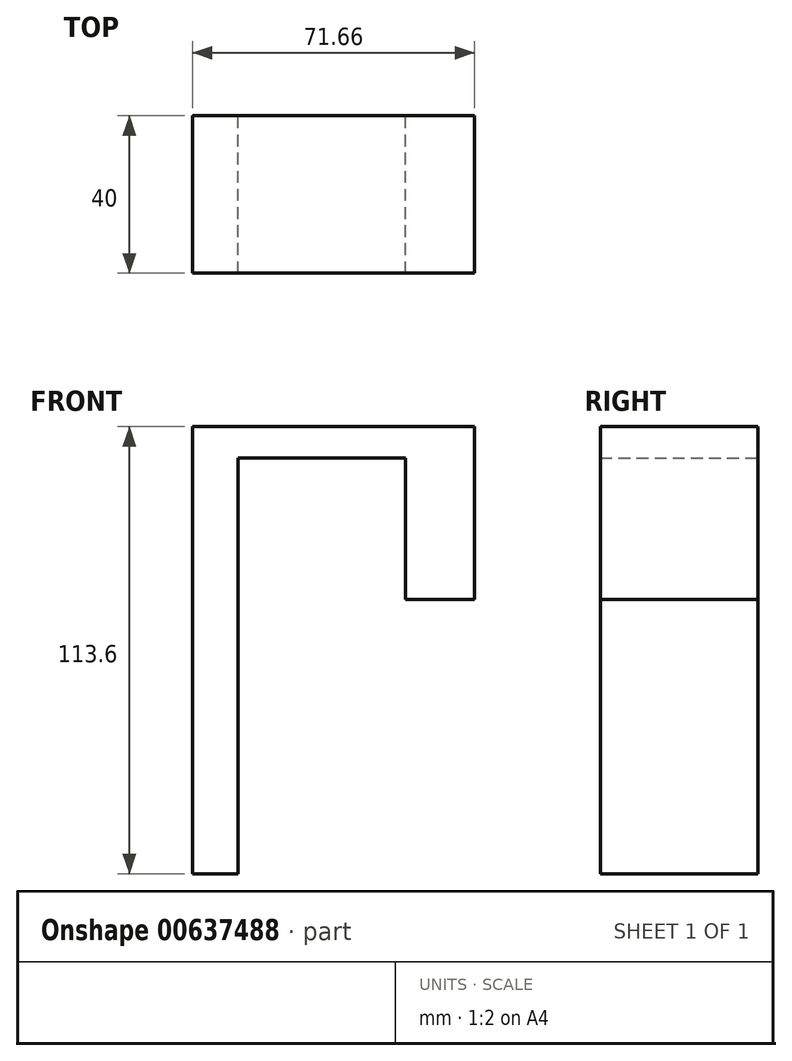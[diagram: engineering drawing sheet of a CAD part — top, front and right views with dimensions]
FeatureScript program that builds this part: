
annotation { "Feature Type Name" : "Feature", "Feature Type Description" : "" }
export const myFeature = defineFeature(function(context is Context, id is Id, definition is map)
    precondition{}
    {
        {
            var Q0;
            Q0=qCreatedBy(makeId("Front.planeOp"),FACE);
            var sketch = newSketch(context, id + "F0", { "sketchPlane" : qUnion([Q0])});
            skLineSegment(sketch, "E0.bottom", {"start": v(-64.44, 45.47) * mm, "end": v(-52.83, 45.47) * mm});
            skLineSegment(sketch, "E0.top", {"start": v(-64.44, -60.2) * mm, "end": v(-52.83, -60.2) * mm});
            skLineSegment(sketch, "E0.left", {"start": v(-64.44, 45.47) * mm, "end": v(-64.44, -60.2) * mm});
            skLineSegment(sketch, "E0.right", {"start": v(-52.83, 45.47) * mm, "end": v(-52.83, -60.2) * mm});
            skLineSegment(sketch, "E1.bottom", {"start": v(-64.44, 45.47) * mm, "end": v(7.22, 45.47) * mm});
            skLineSegment(sketch, "E1.top", {"start": v(-64.44, 53.4) * mm, "end": v(7.22, 53.4) * mm});
            skLineSegment(sketch, "E1.left", {"start": v(-64.44, 45.47) * mm, "end": v(-64.44, 53.4) * mm});
            skLineSegment(sketch, "E1.right", {"start": v(7.22, 45.47) * mm, "end": v(7.22, 53.4) * mm});
            skLineSegment(sketch, "E2.bottom", {"start": v(7.22, 45.47) * mm, "end": v(-10.34, 45.47) * mm});
            skLineSegment(sketch, "E2.top", {"start": v(7.22, 9.49) * mm, "end": v(-10.34, 9.49) * mm});
            skLineSegment(sketch, "E2.left", {"start": v(7.22, 45.47) * mm, "end": v(7.22, 9.49) * mm});
            skLineSegment(sketch, "E2.right", {"start": v(-10.34, 45.47) * mm, "end": v(-10.34, 9.49) * mm});
            skSolve(sketch);
        }
        {
            var Q0;
            Q0 = qSketchRegion(id + "F0", true);
            extrude(context, id + "F1", {"entities" : qUnion([Q0]), "depth" : 40 * mm, "offsetDistance" : 25 * mm});
        }
    });
